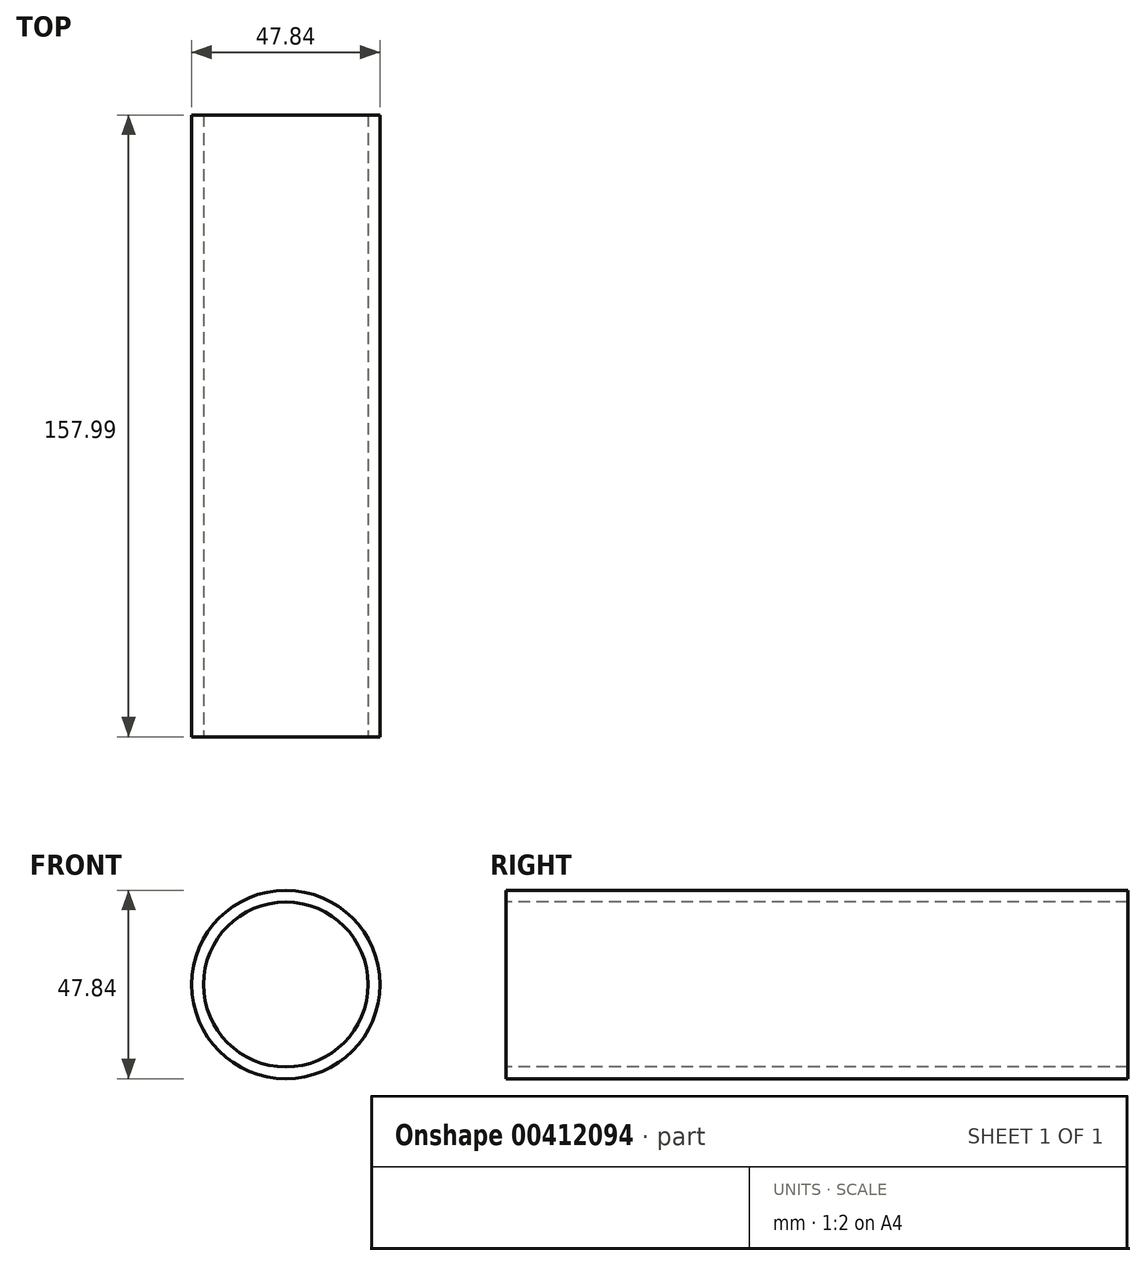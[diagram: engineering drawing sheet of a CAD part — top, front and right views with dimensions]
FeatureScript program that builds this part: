
annotation { "Feature Type Name" : "Feature", "Feature Type Description" : "" }
export const myFeature = defineFeature(function(context is Context, id is Id, definition is map)
    precondition{}
    {
        {
            var Q0;
            Q0=qCreatedBy(makeId("Front.planeOp"),FACE);
            var sketch = newSketch(context, id + "F0", { "sketchPlane" : qUnion([Q0])});
            skCircle(sketch, "E0", {"center": v(-43.59, -50.72) * mm, "radius": 23.92 * mm});
            skCircle(sketch, "E1", {"center": v(-43.59, -50.72) * mm, "radius": 20.93 * mm});
            skSolve(sketch);
        }
        {
            var Q0;
            Q0=sQuery(id+"F0.wireOp",EDGE,"E1");
            var Q1;
            Q1=sQuery(id+"F0.wireOp",EDGE,"E0");
            extrude(context, id + "F1", {"bodyType" : ToolBodyType.SURFACE, "surfaceEntities" : qUnion([Q0, Q1]), "depth" : 158 * mm});
        }
    });
